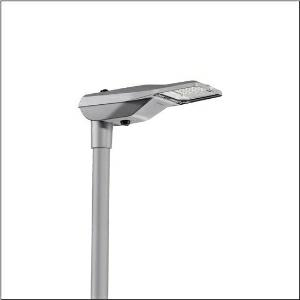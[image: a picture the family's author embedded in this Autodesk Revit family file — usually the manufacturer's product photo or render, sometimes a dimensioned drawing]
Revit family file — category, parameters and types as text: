
# Revit family: streetlight_sl_21_iq_micro___p0_5a_5xe1v31y08cb_657a
name_source: partatom
category: Lighting Fixtures
units: mm (PartAtom-declared; Revit-internal decimal feet)

## family parameters
Cut with Voids When Loaded = No
Host = Face
Light Source = No
Part Type = Normal
Room Calculation Point = No
Round Connector Dimension = Use Diameter
Shared = No

## types (1)
- --- (1 x LED, 2840 lm, 19.1 W, 3000K)
    Apparent Load = 19 VA
    CIE Flux Codes = 37 73 96 100 100
    Color Rendering = 70
    Color Temperature = 3000K
    Default Elevation = 1800 mm
    Description = Streetlight SL 21 iQ micro, mast luminaire, primary light control with lens, of PMMA, primary optical cover: cover, of toughened safety glass, transparent, light distribution: P0.5a, light emission: direct distribution, primary light characteristic: asymmetric, installation type: post-top, side-entry, LED, High Power LED, rated luminous flux: 2.840lm, luminous efficacy: 149lm/W, light colour: 730, colour temperature: 3000K, control gear: iQ-Street Remote, D4i with power reduction, control: pre-setting: logarithmic dimming characteristic, Street-Remote, Auto-Match, Temp-Guard, Lumen-Switch, Night-Set, Smart-Wire, Light-Fading, Desk-Remote (wireless, voltage-free reading and setting of iQ features in the workshop via application-optimized NFC function/RFID function), optimised constant luminous flux control (CLO 2.0), mains connection: 220..240V, AC, 50/60Hz, start of lifetime: 19W, end of service life: 20W, reduction: 9W, luminaire housing, of diecast aluminium, powder-coated, SITECO metallic grey (DB 702S), corrosivity category C5 high according to DIN EN ISO 12944, please order mast flange separately, inclination adjustable: 0°, 5°, 10°, 15°, sealing non-destructively replaceable, multi-level sealing system, length: 528mm, width: 235mm, height: 110mm, mast flange for spigot size: 42mm (side-entry): 5XC10008XM4, 60/48mm (side-entry/post-top): 5XC10108XM2, 76/60mm (side-entry/post-top): 5XC10108XM1, mounting height: 4..8m, Smart Interface below and above, protection rating (complete): IP66, insulation class (complete): insulation class II (safety insulation), certification: CE, ENEC, ENEC+, VDE, impact resistance: IK10, permissible operating ambient temperature for outdoor applications: -40..+50°C, standard-compliant lighting for roads and squares, packaging unit: 1 piece

Light Distribution: P0.5a
    Height = 110 mm
    Lamp = 1 x LED
    Lamp Light Flux = 2840 lm
    Lamp Power = 19.1 W
    Lamp count = 1
    Length = 528 mm
    Luminous efficacy = 149 lm/W
    Manufacturer = Siteco
    ModVariant = No
    Model = 5XE1V31Y08CB
    Number of Poles = 1
    OnlyDefault = Yes
    Power Factor = 1
    Product Name = Streetlight SL 21 iQ micro | P0.5a
    Product group = mast luminaire | pylon top
    ProductGroupID = 6100
    Protection Class = Protection class II
    Protection Degree = IP 66
    RLX_Detail_Level = 1
    RLX_Emergency_Light_Flux = 0 lm
    RLX_Emergency_Type = 0
    RLX_Emergency_Type_DB = No
    RlxData = <blob elided: 97833 chars, md5=23bbaf6e>
    Socket = socket
    Standby Power = 0 W
    System Light Flux = 2840 lm
    System Power = 19 W
    Type Comments = factory setting: luminous flux: 100 % | dim-lin: 254 | 387 mA
    Type Image = l_1007239.jpg
    URL = http://relux.com
    VarID = @adj_077921
    Voltage = 0 V
    Weight = 0.00 kg
    Width = 235 mm

## geometry (parser evidence)
native form markers: Blend x4, Sweep x12
no freeform markers — native parametric forms only
